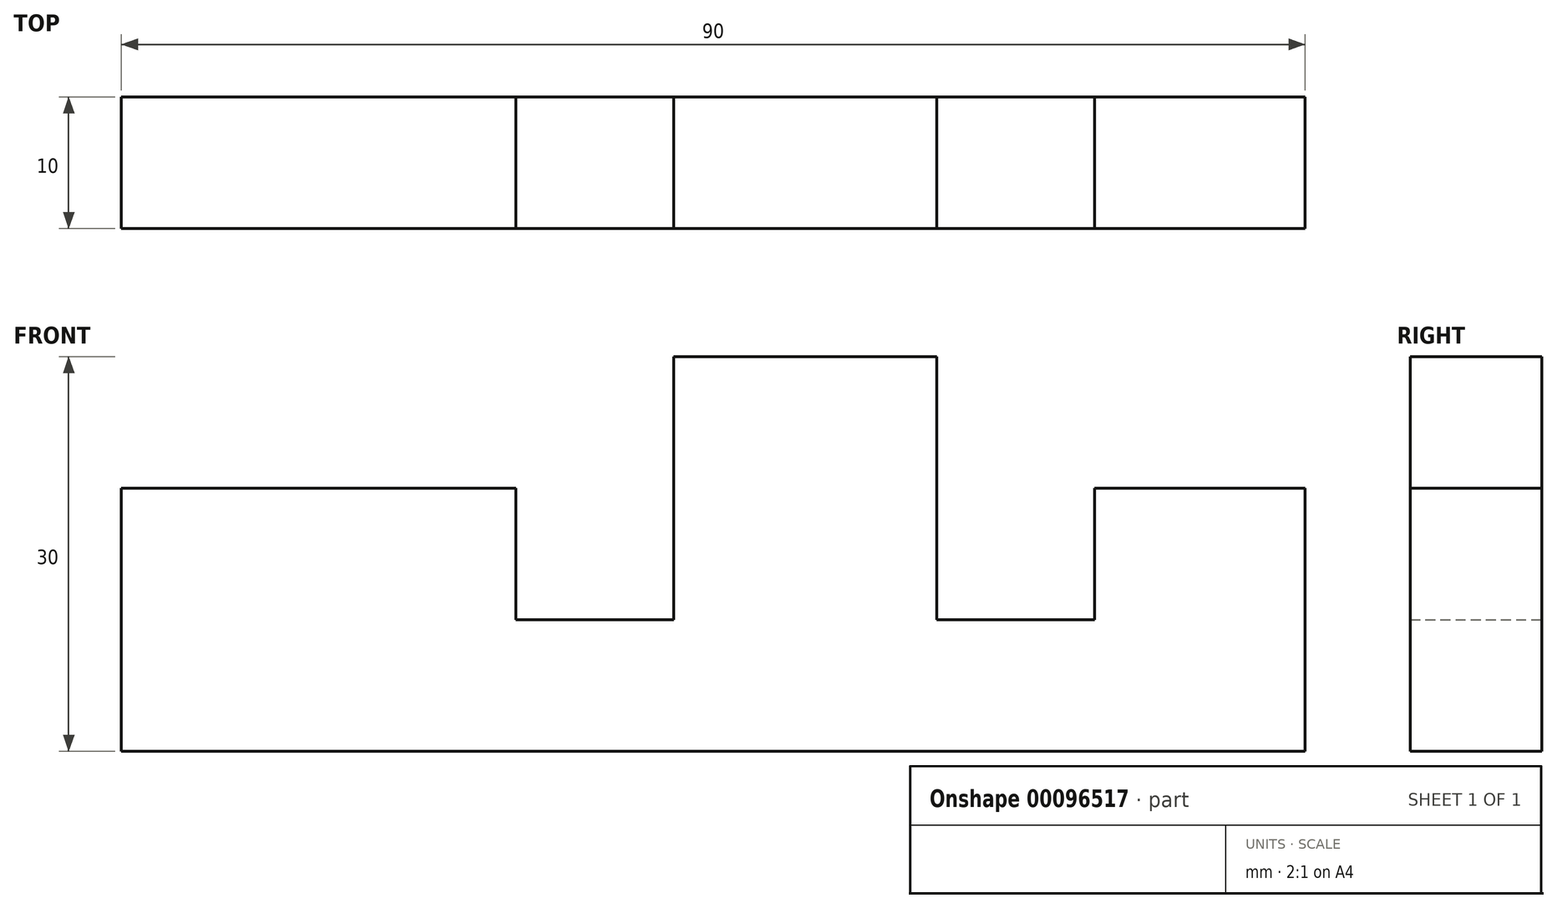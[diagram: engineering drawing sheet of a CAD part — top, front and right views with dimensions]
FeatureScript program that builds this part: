
annotation { "Feature Type Name" : "Feature", "Feature Type Description" : "" }
export const myFeature = defineFeature(function(context is Context, id is Id, definition is map)
    precondition{}
    {
        {
            var Q0;
            Q0=qCreatedBy(makeId("Front.planeOp"),FACE);
            var sketch = newSketch(context, id + "F0", { "sketchPlane" : qUnion([Q0])});
            skLineSegment(sketch, "E0", {"start": v(0, 0) * mm, "end": v(90, 0) * mm});
            skLineSegment(sketch, "E1", {"start": v(0, 0) * mm, "end": v(0, 20) * mm});
            skLineSegment(sketch, "E2", {"start": v(0, 20) * mm, "end": v(30, 20) * mm});
            skLineSegment(sketch, "E3", {"start": v(30, 20) * mm, "end": v(30, 10) * mm});
            skLineSegment(sketch, "E4", {"start": v(30, 10) * mm, "end": v(42, 10) * mm});
            skLineSegment(sketch, "E5", {"start": v(42, 10) * mm, "end": v(42, 30) * mm});
            skLineSegment(sketch, "E6", {"start": v(42, 30) * mm, "end": v(62, 30) * mm});
            skLineSegment(sketch, "E7", {"start": v(62, 30) * mm, "end": v(62, 10) * mm});
            skLineSegment(sketch, "E8", {"start": v(62, 10) * mm, "end": v(74, 10) * mm});
            skLineSegment(sketch, "E9", {"start": v(74, 10) * mm, "end": v(74, 20) * mm});
            skLineSegment(sketch, "E10", {"start": v(90, 0) * mm, "end": v(90, 20) * mm});
            skLineSegment(sketch, "E11", {"start": v(90, 20) * mm, "end": v(74, 20) * mm});
            skSolve(sketch);
        }
        {
            var Q0;
            Q0 = qSketchRegion(id + "F0", true);
            extrude(context, id + "F1", {"entities" : qUnion([Q0]), "depth" : 10 * mm});
        }
    });
